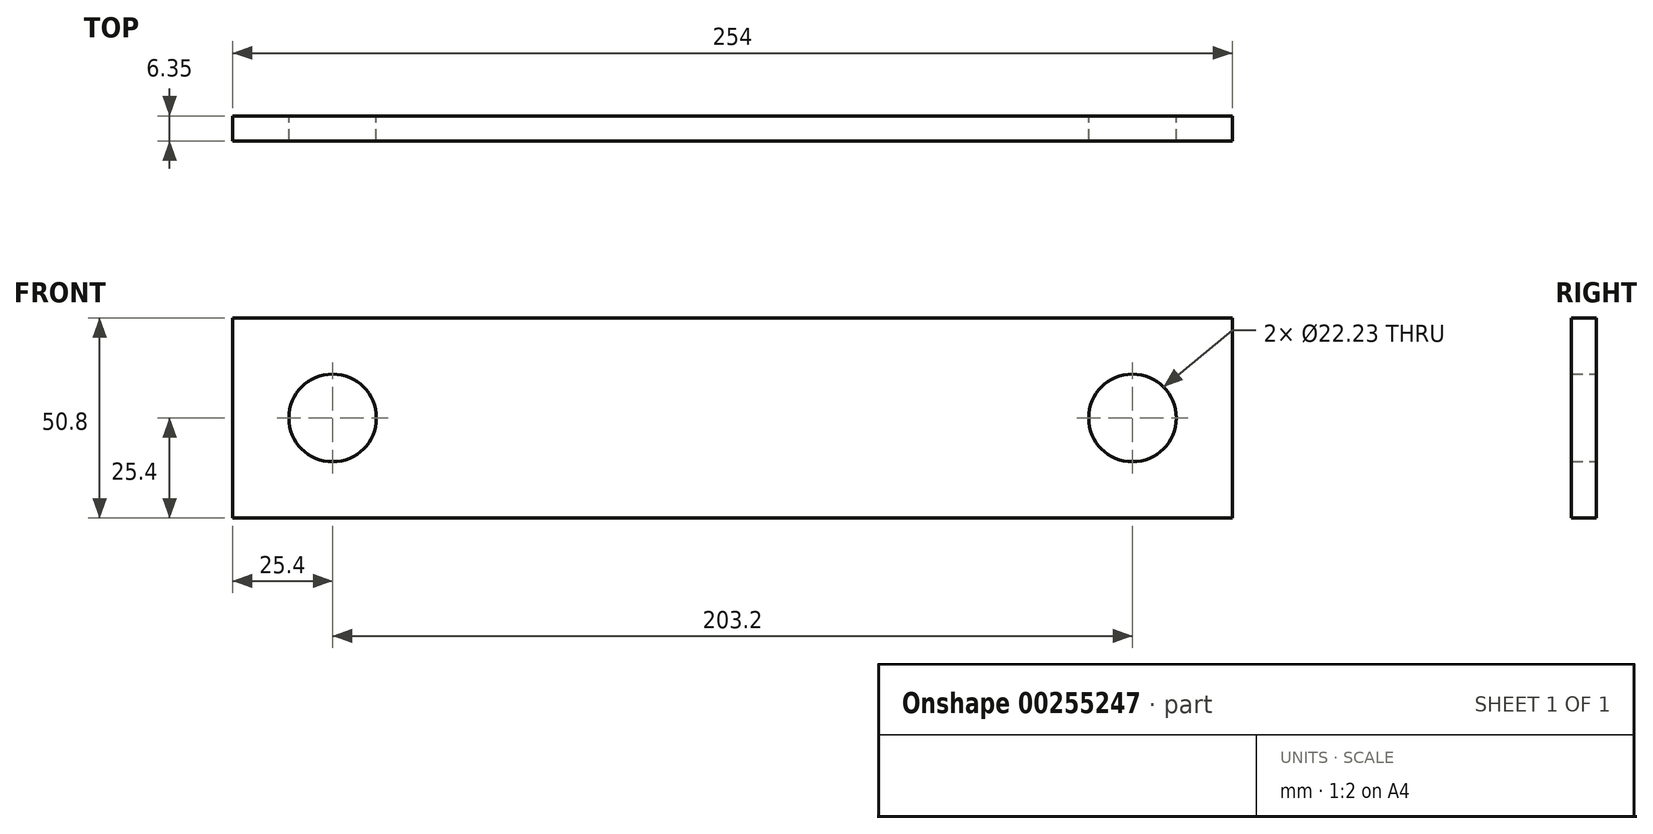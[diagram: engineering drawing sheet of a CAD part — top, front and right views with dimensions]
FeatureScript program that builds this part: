
annotation { "Feature Type Name" : "Feature", "Feature Type Description" : "" }
export const myFeature = defineFeature(function(context is Context, id is Id, definition is map)
    precondition{}
    {
        {
            var Q0;
            Q0=qCreatedBy(makeId("Front.planeOp"),FACE);
            var sketch = newSketch(context, id + "F0", { "sketchPlane" : qUnion([Q0])});
            skLineSegment(sketch, "E0.bottom", {"start": v(127, -25.4) * mm, "end": v(-127, -25.4) * mm});
            skLineSegment(sketch, "E0.top", {"start": v(127, 25.4) * mm, "end": v(-127, 25.4) * mm});
            skLineSegment(sketch, "E0.left", {"start": v(127, -25.4) * mm, "end": v(127, 25.4) * mm});
            skLineSegment(sketch, "E0.right", {"start": v(-127, -25.4) * mm, "end": v(-127, 25.4) * mm});
            skPoint(sketch, "E0.middle", {"position": v(0, 0) * mm});
            skCircle(sketch, "E1", {"center": v(-101.6, 0) * mm, "radius": 11.11 * mm});
            skPoint(sketch, "E1.centerSnap0", {"position": v(-127, 0) * mm});
            skLineSegment(sketch, "E2", {"start": v(0, 25.4) * mm, "end": v(0, -25.4) * mm, "construction": true});
            skCircle(sketch, "E3.MirrorC", {"center": v(101.6, 0) * mm, "radius": 11.11 * mm});
            skSolve(sketch);
        }
        {
            var Q0;
            Q0=makeQuery(id+"F0.imprint","IMPRINT",FACE,{"disambiguationData":[TD([[makeQuery(id+"F0.imprint","IMPRINT",EDGE,{"derivedFrom":sQuery(id+"F0.wireOp",EDGE,"E0.bottom")}),-1.0]])]});
            extrude(context, id + "F1", {"entities" : qUnion([Q0]), "depth" : 6.35 * mm});
        }
    });
